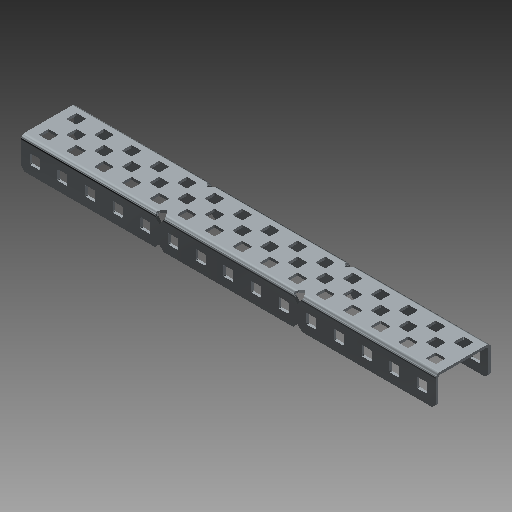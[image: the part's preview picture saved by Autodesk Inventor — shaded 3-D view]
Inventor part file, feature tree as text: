
AUTODESK INVENTOR PART (.ipt)
format: ipt  version: 2018 (Build 220112000, 112)  size: 1,636,864 bytes
history: native  units: mm (DEFAULTED — no unit token found)
features: other x74, extrude x74, pattern_linear x3, sketch x2, imported_body x1, plane x1, mirror x1
ambient origin geometry x8: Origin, YZ Plane, XZ Plane, XY Plane, X Axis, Y Axis, Z Axis, Center Point
bodies: Solid1 (feature_tree)
feature tree (156):
  imported_body  "Base1"
  sketch  "Sketch1"  dims[d1=1.1684mm]
  pattern_linear  "Rectangular Pattern1"  Spacing1=1.1684mm  [1 undecoded]
  pattern_linear  "Rectangular Pattern2"  Spacing1=0.0mm  [1 undecoded]
  pattern_linear  "Rectangular Pattern3"  Count1=15  [1 undecoded]
  plane  "Work Plane1"
  mirror  "Mirror1"
  other  "Srf1"
  other  "Srf2"
  other  "Srf3"
  other  "Srf4"
  other  "Srf5"
  other  "Srf6"
  other  "Srf17"
  other  "Srf18"
  other  "Srf19"
  other  "Srf20"
  other  "Srf21"
  other  "Srf32"
  other  "Srf33"
  other  "Srf34"
  other  "Srf7"
  other  "Srf8"
  other  "Srf9"
  other  "Srf10"
  other  "Srf11"
  other  "Srf12"
  other  "Srf13"
  other  "Srf14"
  other  "Srf15"
  other  "Srf16"
  other  "Srf22"
  other  "Srf23"
  other  "Srf24"
  other  "Srf25"
  other  "Srf26"
  other  "Srf27"
  other  "Srf28"
  other  "Srf29"
  other  "Srf30"
  other  "Srf31"
  other  "Srf35"
  other  "Srf36"
  other  "Srf37"
  other  "Srf38"
  other  "Srf39"
  other  "Srf40"
  other  "Srf41"
  other  "Srf42"
  other  "Srf43"
  other  "Srf44"
  sketch  "Sketch2"  dims[d2=0.0mm d3=1.1684mm d4=0.0mm d5=150.0mm d7=12.7mm d8=20.0mm d10=12.7mm d11=140.0mm d13=12.7mm d14=1.1684mm d15=0.0mm d16=150.0mm d18=12.7mm d19=0.0mm d20=0.0mm d21=0.0mm d22=0.0mm d23=0.0mm d24=0.0mm d25=0.0mm d26=0.0mm d27=0.0mm d28=0.0mm d29=0.0mm d30=0.0mm d31=0.0mm d32=0.0mm d33=0.0mm d34=0.0mm d35=0.0mm d36=0.0mm d37=0.0mm d38=0.0mm d39=0.0mm d40=0.0mm d41=0.0mm d42=0.0mm d43=0.0mm d44=0.0mm d45=0.0mm d46=0.0mm d47=0.0mm d48=0.0mm d49=0.0mm d50=0.0mm d51=0.0mm d52=0.0mm d53=0.0mm d54=0.0mm d55=0.0mm d56=0.0mm d57=0.0mm d58=0.0mm d59=0.0mm d60=0.0mm d61=0.0mm d62=0.0mm d63=0.0mm d64=0.0mm d65=0.0mm d66=0.0mm d67=0.0mm d68=0.0mm d69=0.0mm d70=0.0mm d71=0.0mm d72=0.0mm d73=0.0mm d74=0.0mm d75=0.0mm d76=0.0mm d77=0.0mm d78=0.0mm d79=0.0mm d80=0.0mm d81=0.0mm d82=0.0mm d83=0.0mm d84=0.0mm d85=0.0mm d86=0.0mm d87=0.0mm d88=0.0mm d89=0.0mm d90=0.0mm d91=0.0mm d92=0.0mm d93=0.0mm d94=0.0mm d95=0.0mm d96=0.0mm d97=0.0mm d98=0.0mm d99=0.0mm d100=0.0mm d101=0.0mm d102=0.0mm d103=0.0mm d104=0.0mm d105=0.0mm d106=0.0mm d107=0.0mm d108=0.0mm d109=0.0mm d110=0.0mm d111=0.0mm d112=0.0mm d113=0.0mm d114=0.0mm d115=0.0mm d116=0.0mm d117=0.0mm d118=0.0mm d119=0.0mm d120=0.0mm d121=0.0mm d122=0.0mm d123=0.0mm d124=0.0mm d125=0.0mm d126=0.0mm d127=0.0mm d128=0.0mm d129=0.0mm d130=0.0mm d131=0.0mm d132=0.0mm d133=0.0mm d134=0.0mm d135=0.0mm d136=0.0mm d137=0.0mm d138=0.0mm d139=0.0mm d140=0.0mm d141=0.0mm d142=0.0mm d143=0.0mm d144=0.0mm d145=0.0mm d146=0.0mm d147=0.0mm d148=0.0mm d149=0.0mm d150=0.0mm d151=0.0mm d152=0.0mm d153=0.0mm d154=0.0mm d155=0.0mm d156=0.0mm d157=0.0mm d158=0.0mm d159=0.0mm d160=0.0mm d161=0.0mm d162=0.0mm d163=0.0mm d164=0.0mm d165=0.0mm d166=0.0mm]
  other  "Srf45"
  other  "Srf46"
  other  "Srf47"
  other  "Srf48"
  other  "Srf49"
  other  "Srf50"
  other  "Srf51"
  other  "Srf52"
  other  "Srf53"
  other  "Srf54"
  other  "Srf55"
  other  "Srf56"
  other  "Srf57"
  other  "Srf58"
  other  "Srf59"
  other  "Srf60"
  other  "Srf61"
  other  "Srf62"
  other  "Srf63"
  other  "Srf64"
  other  "Srf65"
  other  "Srf66"
  other  "Srf67"
  other  "Srf68"
  other  "Srf69"
  other  "Srf70"
  other  "Srf71"
  other  "Srf72"
  other  "Srf73"
  other  "Srf74"
  extrude  "ExtrusionSrf1"  Depth=12.7mm
  extrude  "ExtrusionSrf2"  Depth=20.0mm
  extrude  "ExtrusionSrf45"  Depth=140.0mm
  extrude  "ExtrusionSrf3"  Depth=12.7mm
  extrude  "ExtrusionSrf4"  Depth=1.1684mm
  extrude  "ExtrusionSrf5"  TaperAngle=0.0deg  [1 undecoded]
  extrude  "ExtrusionSrf6"  Depth=150.0mm
  extrude  "ExtrusionSrf7"  Depth=12.7mm
  extrude  "ExtrusionSrf8"  [1 undecoded]
  extrude  "ExtrusionSrf9"  [1 undecoded]
  extrude  "ExtrusionSrf10"  [1 undecoded]
  extrude  "ExtrusionSrf11"  [1 undecoded]
  extrude  "ExtrusionSrf12"  [1 undecoded]
  extrude  "ExtrusionSrf13"  [1 undecoded]
  extrude  "ExtrusionSrf14"  [1 undecoded]
  extrude  "ExtrusionSrf15"  [1 undecoded]
  extrude  "ExtrusionSrf16"  [1 undecoded]
  extrude  "ExtrusionSrf17"  [1 undecoded]
  extrude  "ExtrusionSrf18"  [1 undecoded]
  extrude  "ExtrusionSrf19"  [1 undecoded]
  extrude  "ExtrusionSrf20"  [1 undecoded]
  extrude  "ExtrusionSrf21"  [1 undecoded]
  extrude  "ExtrusionSrf22"  [1 undecoded]
  extrude  "ExtrusionSrf23"  [1 undecoded]
  extrude  "ExtrusionSrf24"  [1 undecoded]
  extrude  "ExtrusionSrf25"  [1 undecoded]
  extrude  "ExtrusionSrf26"  [1 undecoded]
  extrude  "ExtrusionSrf27"  [1 undecoded]
  extrude  "ExtrusionSrf28"  [1 undecoded]
  extrude  "ExtrusionSrf29"  [1 undecoded]
  extrude  "ExtrusionSrf30"  [1 undecoded]
  extrude  "ExtrusionSrf31"  [1 undecoded]
  extrude  "ExtrusionSrf32"  [1 undecoded]
  extrude  "ExtrusionSrf33"  [1 undecoded]
  extrude  "ExtrusionSrf34"  [1 undecoded]
  extrude  "ExtrusionSrf35"  [1 undecoded]
  extrude  "ExtrusionSrf36"  [1 undecoded]
  extrude  "ExtrusionSrf37"  [1 undecoded]
  extrude  "ExtrusionSrf38"  [1 undecoded]
  extrude  "ExtrusionSrf39"  [1 undecoded]
  extrude  "ExtrusionSrf40"  [1 undecoded]
  extrude  "ExtrusionSrf41"  [1 undecoded]
  extrude  "ExtrusionSrf42"  [1 undecoded]
  extrude  "ExtrusionSrf43"  [1 undecoded]
  extrude  "ExtrusionSrf44"  [1 undecoded]
  extrude  "ExtrusionSrf46"  [1 undecoded]
  extrude  "ExtrusionSrf47"  [1 undecoded]
  extrude  "ExtrusionSrf48"  [1 undecoded]
  extrude  "ExtrusionSrf49"  [1 undecoded]
  extrude  "ExtrusionSrf50"  [1 undecoded]
  extrude  "ExtrusionSrf51"  [1 undecoded]
  extrude  "ExtrusionSrf52"  [1 undecoded]
  extrude  "ExtrusionSrf53"  [1 undecoded]
  extrude  "ExtrusionSrf54"  [1 undecoded]
  extrude  "ExtrusionSrf55"  [1 undecoded]
  extrude  "ExtrusionSrf56"  [1 undecoded]
  extrude  "ExtrusionSrf57"  [1 undecoded]
  extrude  "ExtrusionSrf58"  [1 undecoded]
  extrude  "ExtrusionSrf59"  [1 undecoded]
  extrude  "ExtrusionSrf60"  [1 undecoded]
  extrude  "ExtrusionSrf61"  [1 undecoded]
  extrude  "ExtrusionSrf62"  [1 undecoded]
  extrude  "ExtrusionSrf63"  [1 undecoded]
  extrude  "ExtrusionSrf64"  [1 undecoded]
  extrude  "ExtrusionSrf65"  [1 undecoded]
  extrude  "ExtrusionSrf66"  [1 undecoded]
  extrude  "ExtrusionSrf67"  [1 undecoded]
  extrude  "ExtrusionSrf68"  [1 undecoded]
  extrude  "ExtrusionSrf69"  [1 undecoded]
  extrude  "ExtrusionSrf70"  [1 undecoded]
  extrude  "ExtrusionSrf71"  [1 undecoded]
  extrude  "ExtrusionSrf72"  [1 undecoded]
  extrude  "ExtrusionSrf73"  [1 undecoded]
  extrude  "ExtrusionSrf74"  [1 undecoded]
note: 70 required parameter values undecoded (feature->parameter linkage not recoverable at this tier; creation-order binding heuristic only, values carry confidence <= 0.55)
